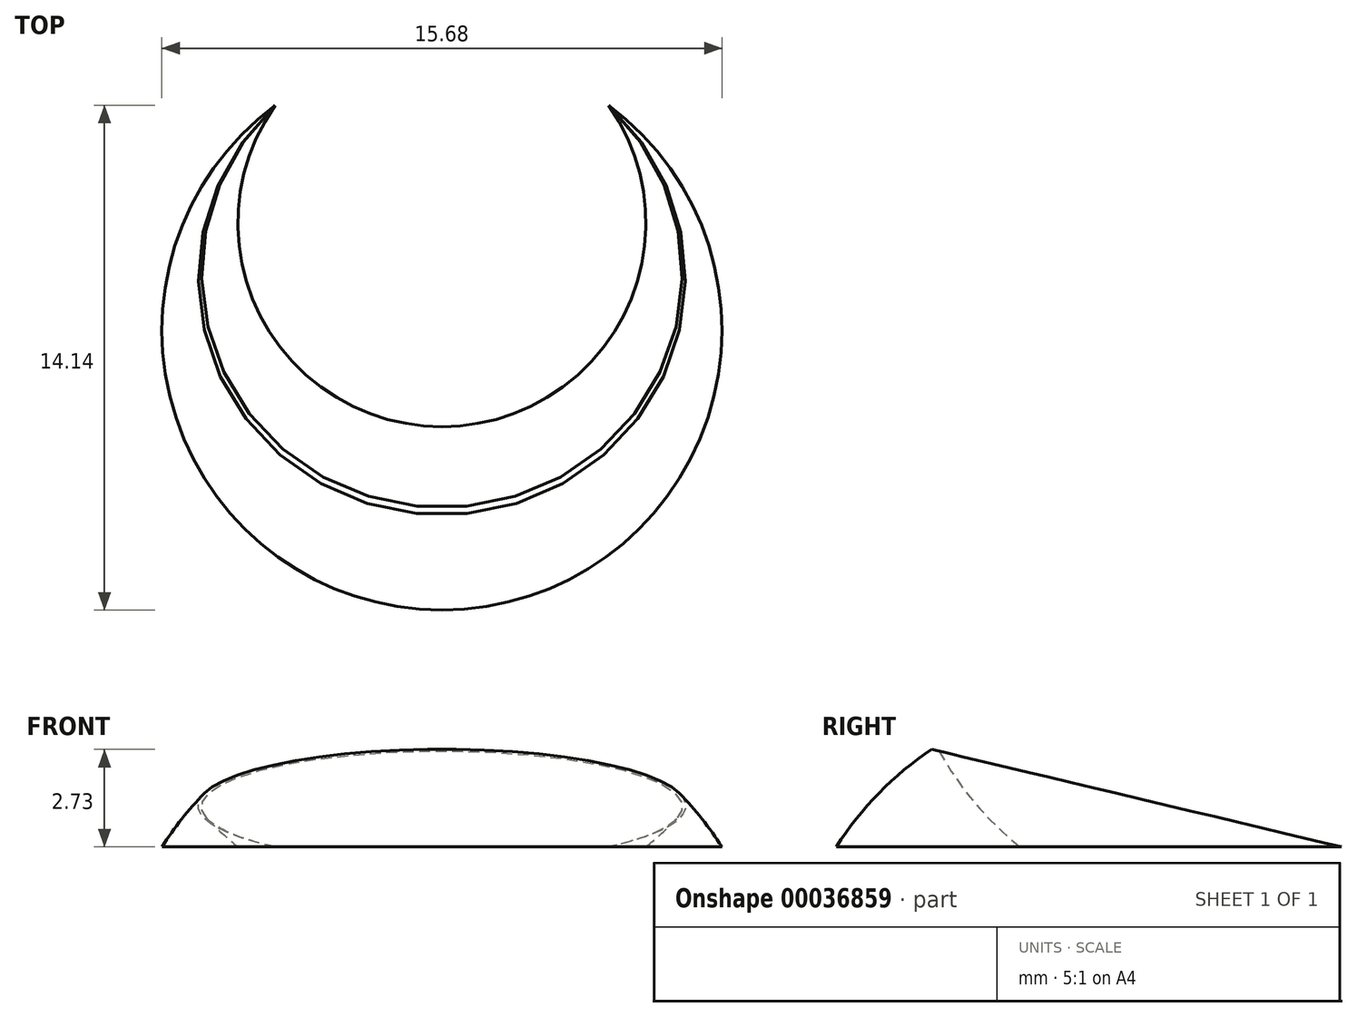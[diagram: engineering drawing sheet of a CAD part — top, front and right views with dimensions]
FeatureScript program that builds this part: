
annotation { "Feature Type Name" : "Feature", "Feature Type Description" : "" }
export const myFeature = defineFeature(function(context is Context, id is Id, definition is map)
    precondition{}
    {
        {
            var Q0;
            Q0=qCreatedBy(makeId("Top.planeOp"),FACE);
            var sketch = newSketch(context, id + "F0", { "sketchPlane" : qUnion([Q0])});
            skLineSegment(sketch, "E0", {"start": v(-4.66, 6.3) * mm, "end": v(0, 0) * mm, "construction": true});
            skLineSegment(sketch, "E1", {"start": v(0, 0) * mm, "end": v(4.66, 6.3) * mm, "construction": true});
            skArc(sketch, "E2", {"start": v(-4.66, 6.3) * mm, "mid": v(0, -7.84) * mm, "end": v(4.66, 6.3) * mm});
            skArc(sketch, "E3", {"start": v(-4.66, 6.3) * mm, "mid": v(0, -2.7) * mm, "end": v(4.66, 6.3) * mm});
            skSolve(sketch);
        }
        {
            var Q0;
            Q0=qCreatedBy(makeId("Front.planeOp"),FACE);
            var sketch = newSketch(context, id + "F1", { "sketchPlane" : qUnion([Q0])});
            skLineSegment(sketch, "E4", {"start": v(0, 0) * mm, "end": v(0, 1.5) * mm, "construction": true});
            skSolve(sketch);
        }
        {
            var Q0;
            Q0=sQuery(id+"F0.wireOp",VERTEX,"E0.start");
            var Q1;
            Q1=sQuery(id+"F0.wireOp",VERTEX,"E1.end");
            var Q2;
            Q2=sQuery(id+"F1.wireOp",VERTEX,"E4.end");
            cPlane(context, id + "F2", {"entities" : qUnion([Q0, Q1, Q2]), "cplaneType" : CPlaneType.THREE_POINT, "offset" : 150 * mm, "width" : 150 * mm, "height" : 150 * mm});
        }
        {
            var Q0;
            Q0=qCreatedBy(id+"F2.planeOp",FACE);
            var sketch = newSketch(context, id + "F3", { "sketchPlane" : qUnion([Q0])});
            skPoint(sketch, "E5.0", {"position": v(-4.66, 6.13) * mm});
            skPoint(sketch, "E6.0", {"position": v(4.66, 6.13) * mm});
            skPoint(sketch, "E7.0", {"position": v(0, 0) * mm});
            skLineSegment(sketch, "E8", {"start": v(0, 0) * mm, "end": v(0, -5.55) * mm, "construction": true});
            skPoint(sketch, "E9.third.point", {"position": v(0, -2.78) * mm});
            skArc(sketch, "E10", {"start": v(-4.66, 6.13) * mm, "mid": v(0, -5.45) * mm, "end": v(4.66, 6.13) * mm});
            skArc(sketch, "E11", {"start": v(-4.66, 6.13) * mm, "mid": v(0, -5.67) * mm, "end": v(4.66, 6.13) * mm});
            skSolve(sketch);
        }
        {
            var Q0;
            Q0=makeQuery(id+"F3.imprint","IMPRINT",FACE,{"disambiguationData":[TD([[makeQuery(id+"F3.imprint","IMPRINT",EDGE,{"derivedFrom":sQuery(id+"F3.wireOp",EDGE,"E10")}),-1.0]])]});
            var Q1;
            Q1=makeQuery(id+"F0.imprint","IMPRINT",FACE,{"disambiguationData":[TD([[makeQuery(id+"F0.imprint","IMPRINT",EDGE,{"derivedFrom":sQuery(id+"F0.wireOp",EDGE,"E2")}),1.0]])]});
            loft(context, id + "F4", {"sheetProfilesArray" : [{ "sheetProfileEntities" : qUnion([Q0]) }, { "sheetProfileEntities" : qUnion([Q1]) }]});
        }
    });
